# Revit family: Albardilla MA (12-22). C-1
name_source: partatom
category: Modelos genéricos
units: mm (PartAtom-declared; Revit-internal decimal feet)

## family parameters
Compartido = No
Corte con vacíos al cargar = No
Cota de conector redondo = Diámetro de uso
Puede alojar armadura = No
Punto de cálculo de habitación = No
Se basa en plano de trabajo = No
Siempre vertical = No
Tipo de pieza = Normal

## types (5) — shared parameters
Altura = 44 mm  [stored 0.144357 ft]
Altura inferior = 29 mm
Descripción = Pieza de hormigón polímero con anclaje de acero inoxidable.
Fabricante = ULMA Architectural Solutions
Material = Hormigón polímero STONEO. Color C-1
URL = https://www.ulmaarchitectural.com
zero-valued in all types: Elevación por defecto

## per-type parameters (varying)
| type | Ancho | Ancho doble | Ancho total | Modelo |
| MA12 | 120 mm  [stored 0.393701 ft] | 30 mm  [stored 0.0984252 ft] | 170 mm  [stored 0.557743 ft] | Albardilla MA12 |
| MA14 | 140 mm  [stored 0.459318 ft] | 35 mm  [stored 0.114829 ft] | 190 mm | Albardilla MA14 |
| MA17 | 170 mm  [stored 0.557743 ft] | 43 mm | 220 mm  [stored 0.721785 ft] | Albardilla MA17 |
| MA22 | 220 mm  [stored 0.721785 ft] | 55 mm  [stored 0.180446 ft] | 270 mm  [stored 0.885827 ft] | Albardilla MA22 |
| MA19 | 190 mm | 48 mm | 240 mm  [stored 0.787402 ft] | Albardilla MA19 |

note: column(s) folded — value = type name in every type: Código de montaje

note: [stored X ft] marks values corroborated as IEEE doubles in the binary element streams (Revit-internal decimal feet)
